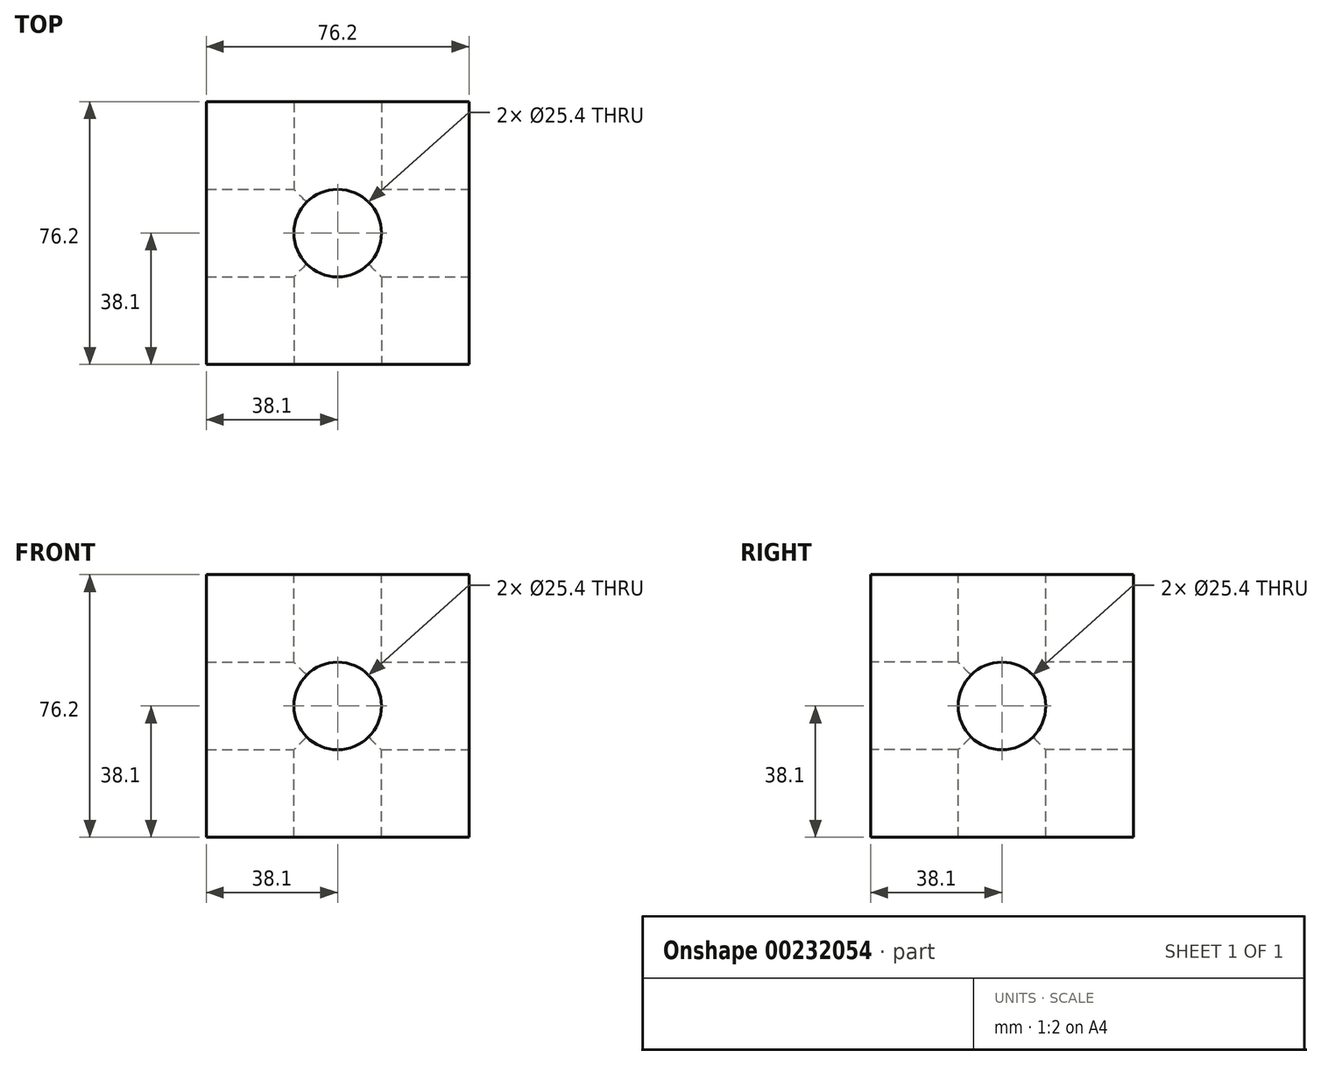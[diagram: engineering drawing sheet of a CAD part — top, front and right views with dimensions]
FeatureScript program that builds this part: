
annotation { "Feature Type Name" : "Feature", "Feature Type Description" : "" }
export const myFeature = defineFeature(function(context is Context, id is Id, definition is map)
    precondition{}
    {
        {
            var Q0;
            Q0=qCreatedBy(makeId("Right.planeOp"),FACE);
            var sketch = newSketch(context, id + "F6", { "sketchPlane" : qUnion([Q0])});
            skLineSegment(sketch, "E0.bottom", {"start": v(38.1, 38.1) * mm, "end": v(-38.1, 38.1) * mm});
            skLineSegment(sketch, "E0.top", {"start": v(38.1, -38.1) * mm, "end": v(-38.1, -38.1) * mm});
            skLineSegment(sketch, "E0.left", {"start": v(38.1, 38.1) * mm, "end": v(38.1, -38.1) * mm});
            skLineSegment(sketch, "E0.right", {"start": v(-38.1, 38.1) * mm, "end": v(-38.1, -38.1) * mm});
            skPoint(sketch, "E0.middle", {"position": v(0, 0) * mm});
            skSolve(sketch);
        }
        {
            var Q0;
            Q0=makeQuery(id+"F6.imprint","IMPRINT",FACE,{"disambiguationData":[TD([[makeQuery(id+"F6.imprint","IMPRINT",EDGE,{"derivedFrom":sQuery(id+"F6.wireOp",EDGE,"E0.bottom")}),1.0]])]});
            extrude(context, id + "F0", {"entities" : qUnion([Q0]), "oppositeDirection" : true, "depth" : 76.2 * mm});
        }
        {
            var Q0;
            Q0=makeQuery(id+"F0.opExtrude","SWEPT_FACE",FACE,{"disambiguationData":[OSD([sQuery(id+"F6.wireOp",EDGE,"E0.bottom")])]});
            var sketch = newSketch(context, id + "F7", { "sketchPlane" : qUnion([Q0])});
            skPoint(sketch, "E1", {"position": v(-38.1, 0) * mm});
            skPoint(sketch, "E1.positionSnap0", {"position": v(-38.1, 38.1) * mm});
            skSolve(sketch);
        }
        {
            var Q0;
            Q0=sQuery(id+"F7.wireOp",VERTEX,"E1");
            var Q1;
            Q1=makeQuery(id+"F0.opExtrude","SWEPT_BODY",BODY,{"disambiguationData":[OSD([sQuery(id+"F6.wireOp",EDGE,"E0.bottom"),sQuery(id+"F6.wireOp",EDGE,"E0.top"),sQuery(id+"F6.wireOp",EDGE,"E0.left"),sQuery(id+"F6.wireOp",EDGE,"E0.right")])]});
            hole(context, id + "F1", {"style" : HoleStyle.SIMPLE, "endStyle" : HoleEndStyle.THROUGH, "holeDiameter" : 25.4 * mm, "locations" : qUnion([Q0]), "scope" : qUnion([Q1]), "isTappedThrough" : true});
        }
        {
            var Q0;
            Q0=makeQuery(id+"F0.opExtrude","SWEPT_FACE",FACE,{"disambiguationData":[OSD([sQuery(id+"F6.wireOp",EDGE,"E0.right")])]});
            var sketch = newSketch(context, id + "F2", { "sketchPlane" : qUnion([Q0])});
            skPoint(sketch, "E2", {"position": v(-38.1, 0) * mm});
            skPoint(sketch, "E2.positionSnap0", {"position": v(-38.1, 38.1) * mm});
            skSolve(sketch);
        }
        {
            var Q0;
            Q0=sQuery(id+"F2.wireOp",VERTEX,"E2");
            var Q1;
            Q1=makeQuery(id+"F0.opExtrude","SWEPT_BODY",BODY,{"disambiguationData":[OSD([sQuery(id+"F6.wireOp",EDGE,"E0.bottom"),sQuery(id+"F6.wireOp",EDGE,"E0.top"),sQuery(id+"F6.wireOp",EDGE,"E0.left"),sQuery(id+"F6.wireOp",EDGE,"E0.right")])]});
            hole(context, id + "F8", {"style" : HoleStyle.SIMPLE, "endStyle" : HoleEndStyle.THROUGH, "holeDiameter" : 25.4 * mm, "locations" : qUnion([Q0]), "scope" : qUnion([Q1]), "isTappedThrough" : true});
        }
        {
            var Q0;
            Q0=makeQuery(id+"F0.opExtrude","CAP_FACE",FACE,{"disambiguationData":[OSD([sQuery(id+"F6.wireOp",EDGE,"E0.bottom"),sQuery(id+"F6.wireOp",EDGE,"E0.top"),sQuery(id+"F6.wireOp",EDGE,"E0.left"),sQuery(id+"F6.wireOp",EDGE,"E0.right")])],"isStart":true});
            var sketch = newSketch(context, id + "F3", { "sketchPlane" : qUnion([Q0])});
            skPoint(sketch, "E3", {"position": v(0, 0) * mm});
            skSolve(sketch);
        }
        {
            var Q0;
            Q0=sQuery(id+"F3.wireOp",VERTEX,"E3");
            var Q1;
            Q1=makeQuery(id+"F0.opExtrude","SWEPT_BODY",BODY,{"disambiguationData":[OSD([sQuery(id+"F6.wireOp",EDGE,"E0.bottom"),sQuery(id+"F6.wireOp",EDGE,"E0.top"),sQuery(id+"F6.wireOp",EDGE,"E0.left"),sQuery(id+"F6.wireOp",EDGE,"E0.right")])]});
            hole(context, id + "F4", {"style" : HoleStyle.SIMPLE, "endStyle" : HoleEndStyle.THROUGH, "holeDiameter" : 25.4 * mm, "locations" : qUnion([Q0]), "scope" : qUnion([Q1]), "isTappedThrough" : true});
        }
    });
